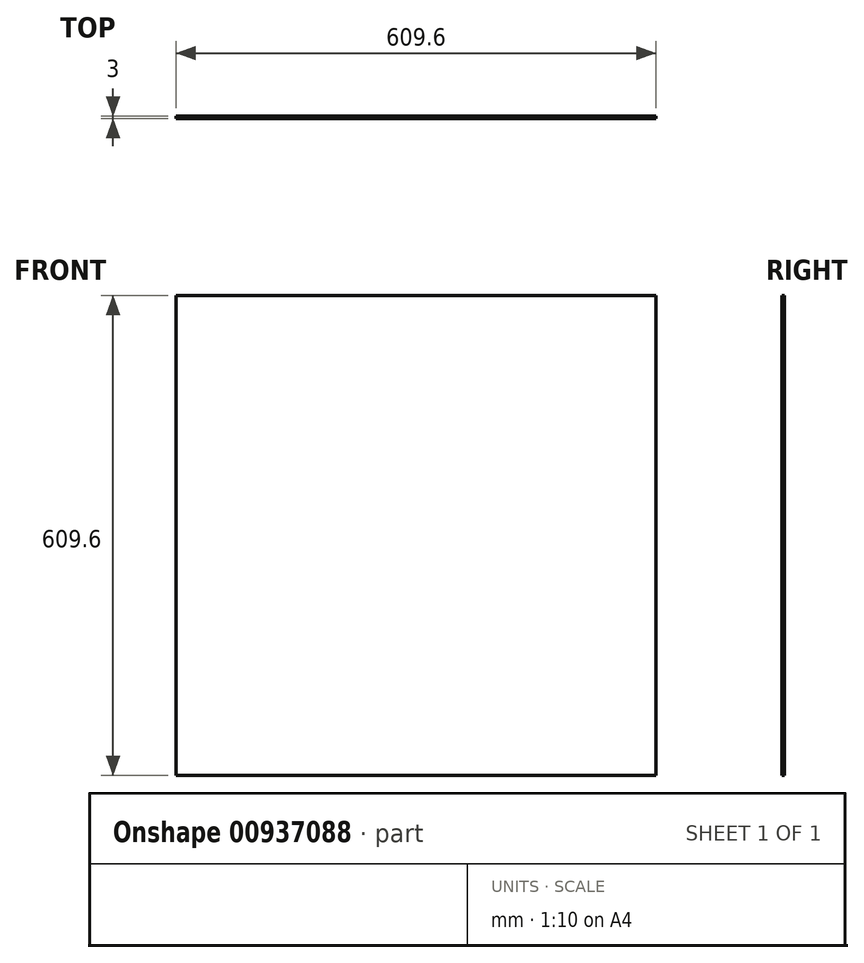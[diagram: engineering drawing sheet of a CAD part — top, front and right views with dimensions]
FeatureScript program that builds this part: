
annotation { "Feature Type Name" : "Feature", "Feature Type Description" : "" }
export const myFeature = defineFeature(function(context is Context, id is Id, definition is map)
    precondition{}
    {
        {
            var Q0;
            Q0=qCreatedBy(makeId("Front.planeOp"),FACE);
            var sketch = newSketch(context, id + "F0", { "sketchPlane" : qUnion([Q0])});
            skLineSegment(sketch, "E0.bottom", {"start": v(332.65, 497.93) * mm, "end": v(-276.95, 497.93) * mm});
            skLineSegment(sketch, "E0.top", {"start": v(332.65, -111.67) * mm, "end": v(-276.95, -111.67) * mm});
            skLineSegment(sketch, "E0.left", {"start": v(332.65, 497.93) * mm, "end": v(332.65, -111.67) * mm});
            skLineSegment(sketch, "E0.right", {"start": v(-276.95, 497.93) * mm, "end": v(-276.95, -111.67) * mm});
            skSolve(sketch);
        }
        {
            var Q0;
            Q0 = qSketchRegion(id + "F0", true);
            extrude(context, id + "F1", {"entities" : qUnion([Q0]), "depth" : 3 * mm, "offsetDistance" : 25 * mm});
        }
    });
